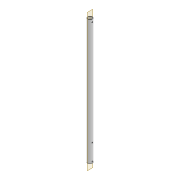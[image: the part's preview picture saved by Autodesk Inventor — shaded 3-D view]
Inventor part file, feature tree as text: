
AUTODESK INVENTOR PART (.ipt)
format: ipt  version: 2022 (Build 260153000, 153)  size: 106,496 bytes
history: native  units: mm
features: extrude x2, sketch x2
ambient origin geometry x8: Origin, YZ Plane, XZ Plane, XY Plane, X Axis, Y Axis, Z Axis, Center Point
bodies: Solid1 (feature_tree)
feature tree (4):
  extrude  "Extrusion1"  Depth=10.0mm
  extrude  "Extrusion2"  Depth=46.0mm
  sketch  "Sketch1"  dims[d0=12.0mm d1=10.0mm]
  sketch  "Sketch2"  dims[d2=320.0mm d3=0.0mm d4=3.0mm d5=3.0mm d6=4.0mm d7=46.0mm d8=320.0mm d9=0.0mm d10=3.0mm d11=6.5mm]
